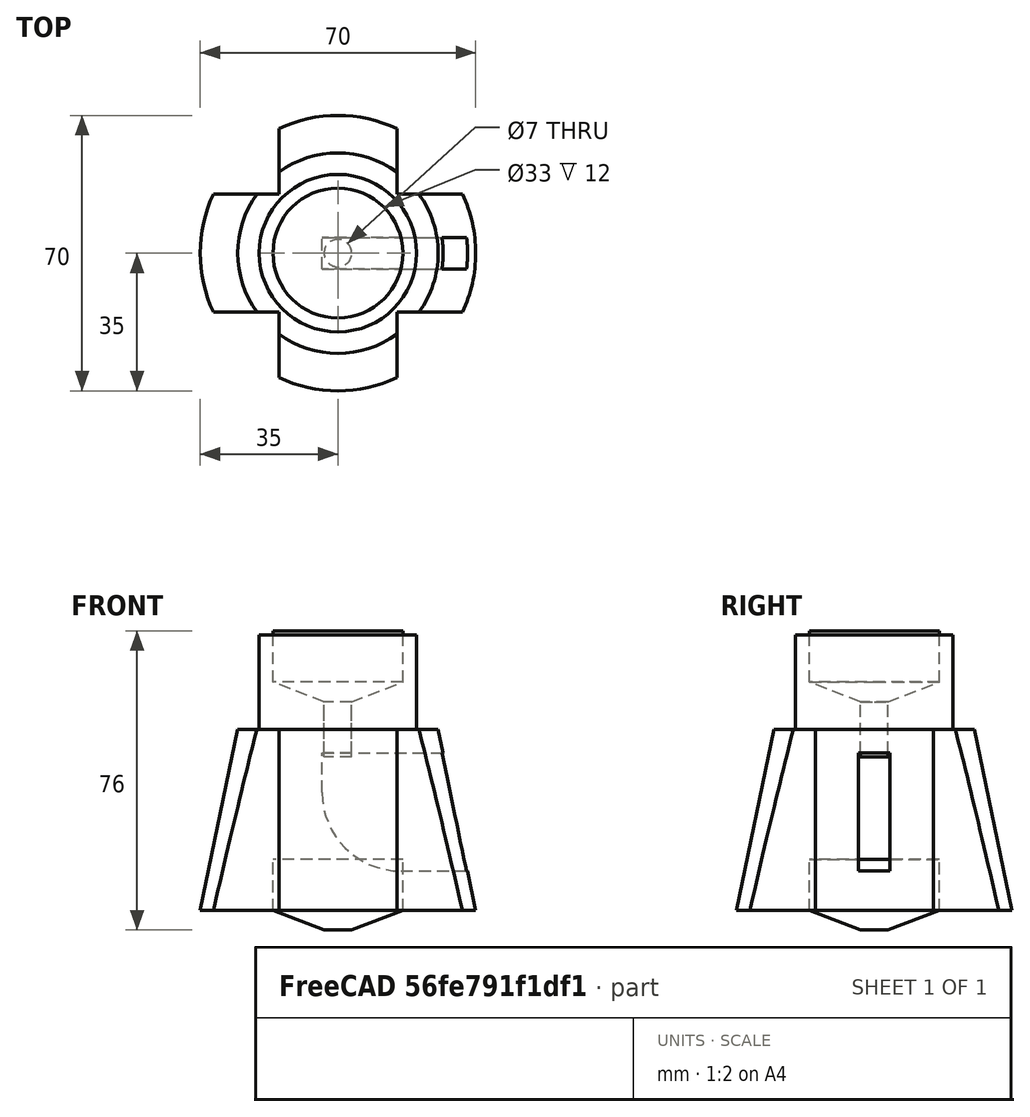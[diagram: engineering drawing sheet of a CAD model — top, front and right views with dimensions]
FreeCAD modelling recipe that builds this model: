
FCSTD DOCUMENT  (FreeCAD 0.18.3R)
Label: Soporte deposito
License: All rights reserved
LicenseURL: http://en.wikipedia.org/wiki/All_rights_reserved
objects: Part::Cylinder×4, Part::MultiFuse×4, Part::Feature×3, Part::Box×3, Part::Cut×3, Part::Cone×2, Part::Fuse×1, Part::FeaturePython×1, Part::Fillet×1
note: 22 computed .brp shape members not serialized (recipe doc carries the construction recipe); baked Part::Feature solids carry a one-line shape summary decoded from their .brp

FEATURE [Part::Cylinder] Cylinder  label="Cilindro"
  Angle = 360
  AttacherType = Attacher::AttachEngine3D
  Height = 13
  Radius = 16.5
FEATURE [Part::Cone] Cone  label="Cono"
  Angle = 360
  AttacherType = Attacher::AttachEngine3D
  Height = 5
  Placement = pos=(0,0,-5) rot=(0,0,1;0rad)
  Radius1 = 3.5
  Radius2 = 16.5
FEATURE [Part::MultiFuse] Fusion
  Shapes = -> [Cone,Cylinder]
FEATURE [Part::Feature] Fusion001  label="MoldeTapon"
  Placement = pos=(0,0,58) rot=(0,0,1;0rad)
  shape: bbox 33 x 33 x 18 mm, 4 faces (baked)
FEATURE [Part::Cone] Cone001  label="Cono001"
  Angle = 360
  AttacherType = Attacher::AttachEngine3D
  Height = 70
  Radius1 = 35
  Radius2 = 20.5
FEATURE [Part::Cylinder] Cylinder001  label="Cilindro001"
  Angle = 360
  AttacherType = Attacher::AttachEngine3D
  Height = 15
  Placement = pos=(0,0,39) rot=(0,0,1;0rad)
  Radius = 3.5
FEATURE [Part::Fuse] Fusion002
  Base = -> Fusion001
  Tool = -> Cylinder001
FEATURE [Part::Feature] Fusion002001  label="Fusion003"
  shape: bbox 33 x 33 x 32 mm, 5 faces (baked)
FEATURE [Part::Box] Box  label="Cubo"
  AttacherType = Attacher::AttachEngine3D
  Height = 30
  Length = 60
  Placement = pos=(-4,-4,10) rot=(0,0,1;0rad)
  Width = 8
FEATURE [Part::Box] Box001  label="Cubo001"
  AttacherType = Attacher::AttachEngine3D
  Height = 22
  Length = 10
  Placement = pos=(46,-10,10) rot=(0,0,1;0rad)
  Width = 20
FEATURE [Part::MultiFuse] Fusion002002
  Shapes = -> [Box,Box001]
FEATURE [Part::Box] Box002  label="Cubo002"
  AttacherType = Attacher::AttachEngine3D
  Height = 55
  Length = 45
  Width = 45
FEATURE [Part::FeaturePython] Array  # Draft array (typed FeaturePython)
  Angle = 360
  ArrayType = 0
  Axis = (0,0,1)
  Base = -> Box002
  Center = (0,0,0)
  Fuse = false
  IntervalAxis = (1,0,0)
  IntervalX = (75,0,0)
  IntervalY = (0,75,0)
  IntervalZ = (0,0,1)
  NumberPolar = 1
  NumberX = 2
  NumberY = 2
  NumberZ = 1
  Placement = pos=(-60,-60,-1) rot=(0,0,1;0rad)
FEATURE [Part::MultiFuse] Fusion002003
  Shapes = -> [Fusion002001,Fusion002002]
FEATURE [Part::Cut] Cut
  Base = -> Cone001
  Tool = -> Fusion002003
FEATURE [Part::Cylinder] Cylinder002  label="Cilindro002"
  Angle = 360
  AttacherType = Attacher::AttachEngine3D
  Height = 30
  Placement = pos=(0,0,-1) rot=(0,0,1;0rad)
  Radius = 20
FEATURE [Part::Cylinder] Cylinder003  label="Cilindro003"
  Angle = 360
  AttacherType = Attacher::AttachEngine3D
  Height = 25
  Radius = 30
FEATURE [Part::Cut] Cut002
  Base = -> Cylinder003
  Placement = pos=(0,0,46) rot=(0,0,1;0rad)
  Tool = -> Cylinder002
FEATURE [Part::MultiFuse] Fusion002004
  Shapes = -> [Cut002,Array]
FEATURE [Part::Cut] Cut003
  Base = -> Cut
  Tool = -> Fusion002004
FEATURE [Part::Fillet] Fillet
  Base = -> Cut003
  Edges = 1 edges r=20: [Edge18]
FEATURE [Part::Feature] Fillet001
  shape: bbox 70 x 70 x 70 mm, 26 faces (baked)
